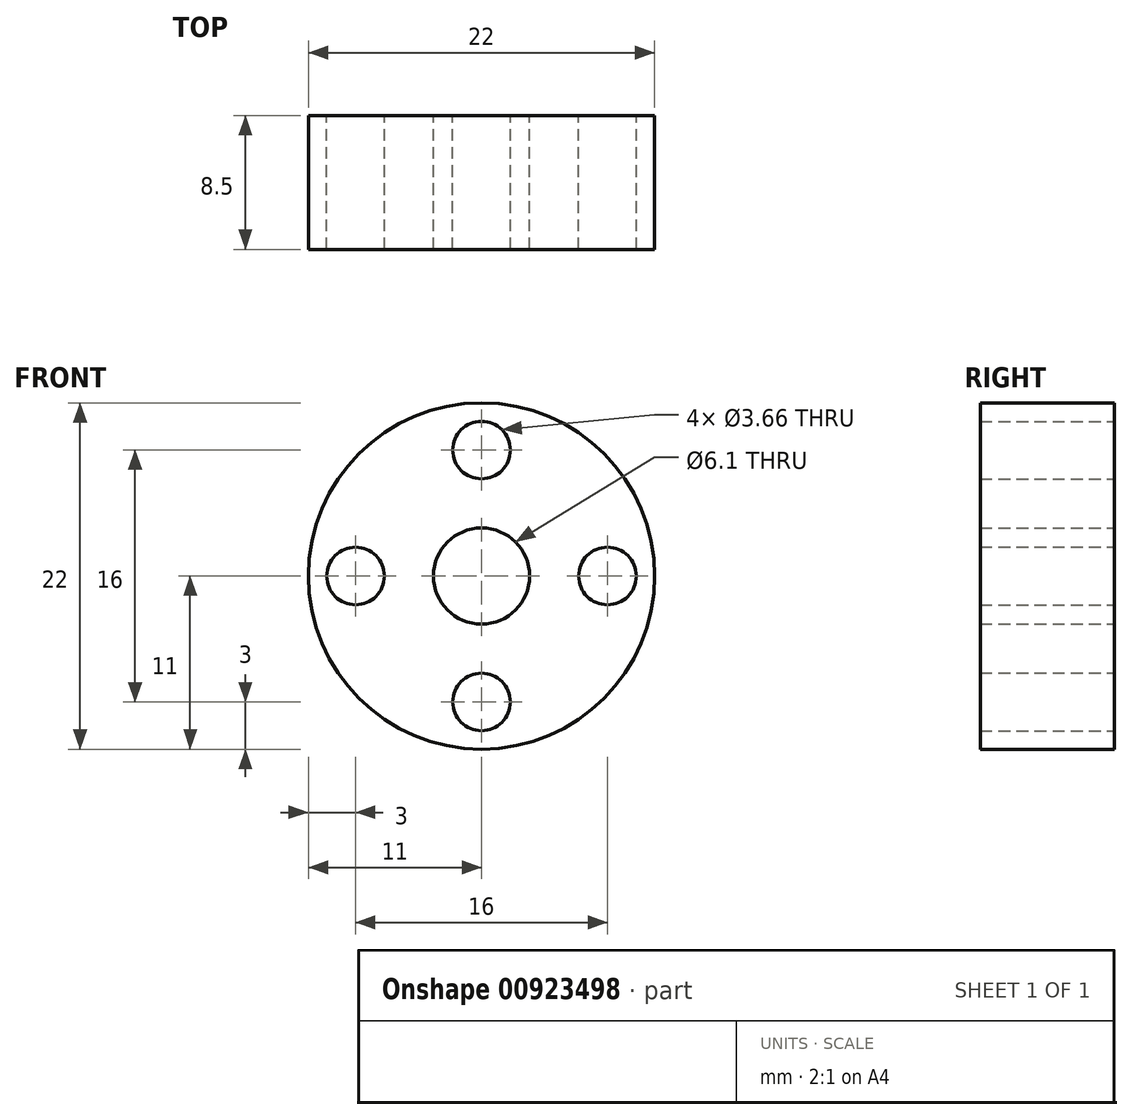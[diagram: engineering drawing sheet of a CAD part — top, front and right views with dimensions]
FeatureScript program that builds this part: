
annotation { "Feature Type Name" : "Feature", "Feature Type Description" : "" }
export const myFeature = defineFeature(function(context is Context, id is Id, definition is map)
    precondition{}
    {
        {
            var Q0;
            Q0=qCreatedBy(makeId("Front.planeOp"),FACE);
            var sketch = newSketch(context, id + "F0", { "sketchPlane" : qUnion([Q0])});
            skCircle(sketch, "E0", {"center": v(0, 0) * mm, "radius": 11 * mm});
            skLineSegment(sketch, "E1.bottom", {"start": v(5.66, 5.66) * mm, "end": v(-5.66, 5.66) * mm, "construction": true});
            skLineSegment(sketch, "E1.top", {"start": v(5.66, -5.66) * mm, "end": v(-5.66, -5.66) * mm, "construction": true});
            skLineSegment(sketch, "E1.left", {"start": v(5.66, 5.66) * mm, "end": v(5.66, -5.66) * mm, "construction": true});
            skLineSegment(sketch, "E1.right", {"start": v(-5.66, 5.66) * mm, "end": v(-5.66, -5.66) * mm, "construction": true});
            skCircle(sketch, "E2", {"center": v(-5.66, 5.66) * mm, "radius": 1.83 * mm});
            skCircle(sketch, "E3", {"center": v(5.66, 5.66) * mm, "radius": 1.83 * mm});
            skCircle(sketch, "E4", {"center": v(5.66, -5.66) * mm, "radius": 1.83 * mm});
            skCircle(sketch, "E5", {"center": v(-5.66, -5.66) * mm, "radius": 1.83 * mm});
            skCircle(sketch, "E6", {"center": v(0, 0) * mm, "radius": 3.05 * mm});
            skSolve(sketch);
        }
        {
            var Q0;
            Q0=qSketchRegion(id+"F0",true);
            extrude(context, id + "F1", {"entities" : qUnion([Q0]), "depth" : 8.5 * mm, "offsetDistance" : 25 * mm});
        }
        {
            var Q0;
            Q0=makeQuery(id+"F1.opExtrude","SWEPT_BODY",BODY,{"disambiguationData":[OSD([sQuery(id+"F0.wireOp",EDGE,"E0"),sQuery(id+"F0.wireOp",EDGE,"E2"),sQuery(id+"F0.wireOp",EDGE,"E3"),sQuery(id+"F0.wireOp",EDGE,"E4"),sQuery(id+"F0.wireOp",EDGE,"E5"),sQuery(id+"F0.wireOp",EDGE,"E6")])]});
            var Q1;
            Q1=makeQuery(id+"F1.opExtrude","CAP_EDGE",EDGE,{"disambiguationData":[OSD([sQuery(id+"F0.wireOp",EDGE,"E6")])],"isStart":true});
            transform(context, id + "F2", {"entities" : qUnion([Q0]), "transformType" : TransformType.ROTATION, "transformAxis" : qUnion([Q1]), "angle" : 45 * degree, "makeCopy" : false});
        }
    });
